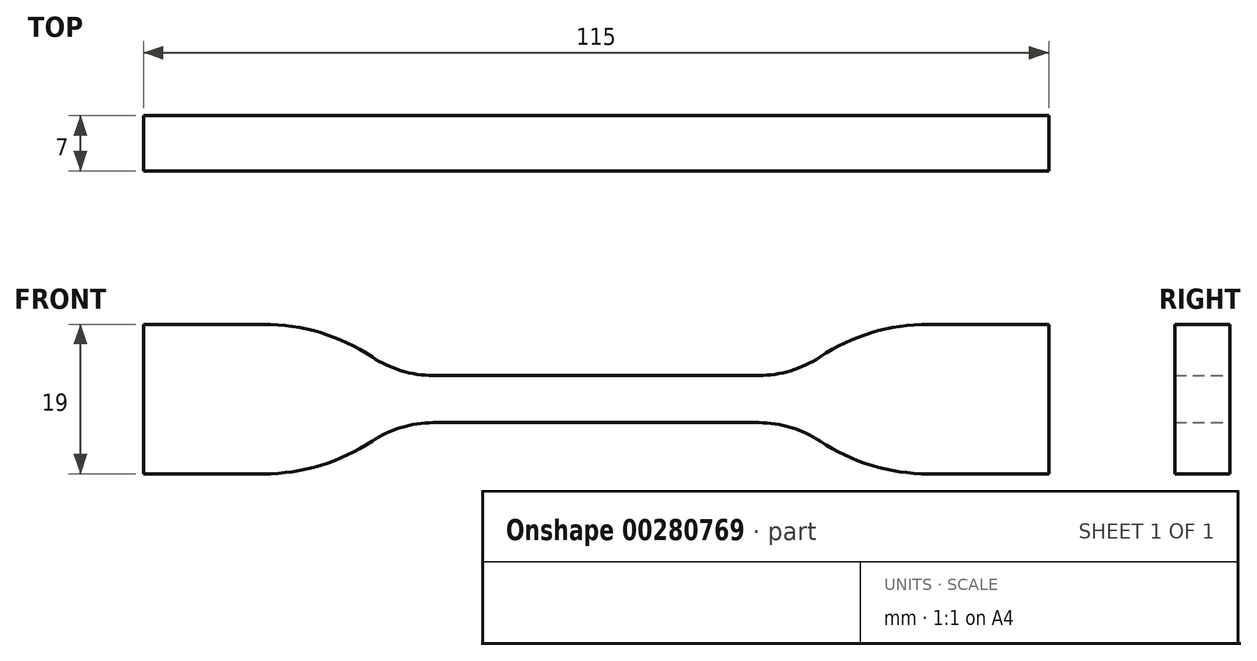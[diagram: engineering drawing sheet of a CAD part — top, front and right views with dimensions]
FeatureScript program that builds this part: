
annotation { "Feature Type Name" : "Feature", "Feature Type Description" : "" }
export const myFeature = defineFeature(function(context is Context, id is Id, definition is map)
    precondition{}
    {
        {
            var Q0;
            Q0=qCreatedBy(makeId("Front.planeOp"),FACE);
            var sketch = newSketch(context, id + "F0", { "sketchPlane" : qUnion([Q0])});
            skLineSegment(sketch, "E0", {"start": v(0, 3) * mm, "end": v(20.68, 3) * mm});
            skArc(sketch, "E1", {"start": v(20.68, 3) * mm, "mid": v(24.72, 3.6) * mm, "end": v(28.42, 5.33) * mm});
            skLineSegment(sketch, "E2", {"start": v(57.5, 9.5) * mm, "end": v(42.24, 9.5) * mm});
            skLineSegment(sketch, "E3.MirrorCS", {"start": v(57.5, -9.5) * mm, "end": v(42.24, -9.5) * mm});
            skLineSegment(sketch, "E4.MirrorCS", {"start": v(0, -3) * mm, "end": v(20.68, -3) * mm});
            skArc(sketch, "E5.MirrorCS", {"start": v(20.68, -3) * mm, "mid": v(24.72, -3.6) * mm, "end": v(28.42, -5.33) * mm});
            skLineSegment(sketch, "E6", {"start": v(57.5, 9.5) * mm, "end": v(57.5, -9.5) * mm});
            skLineSegment(sketch, "E7.MirrorCS", {"start": v(0, 3) * mm, "end": v(-20.68, 3) * mm});
            skArc(sketch, "E8.MirrorCS", {"start": v(-20.68, 3) * mm, "mid": v(-24.72, 3.6) * mm, "end": v(-28.42, 5.33) * mm});
            skLineSegment(sketch, "E9.MirrorCS", {"start": v(-57.5, 9.5) * mm, "end": v(-42.24, 9.5) * mm});
            skLineSegment(sketch, "E10.MirrorCS", {"start": v(-57.5, -9.5) * mm, "end": v(-42.24, -9.5) * mm});
            skLineSegment(sketch, "E11.MirrorCS", {"start": v(-57.5, 9.5) * mm, "end": v(-57.5, -9.5) * mm});
            skLineSegment(sketch, "E12.MirrorCS", {"start": v(0, -3) * mm, "end": v(-20.68, -3) * mm});
            skArc(sketch, "E13.MirrorCS", {"start": v(-20.68, -3) * mm, "mid": v(-24.72, -3.6) * mm, "end": v(-28.42, -5.33) * mm});
            skPoint(sketch, "E14.visualSharp", {"position": v(-32.5, -9.5) * mm});
            skArc(sketch, "E14.filletArc", {"start": v(-42.24, -9.5) * mm, "mid": v(-35.02, -8.44) * mm, "end": v(-28.42, -5.33) * mm});
            skPoint(sketch, "E15.visualSharp", {"position": v(-32.5, 9.5) * mm});
            skArc(sketch, "E15.filletArc", {"start": v(-28.42, 5.33) * mm, "mid": v(-35.02, 8.44) * mm, "end": v(-42.24, 9.5) * mm});
            skPoint(sketch, "E16.visualSharp", {"position": v(32.5, 9.5) * mm});
            skArc(sketch, "E16.filletArc", {"start": v(42.24, 9.5) * mm, "mid": v(35.02, 8.44) * mm, "end": v(28.42, 5.33) * mm});
            skPoint(sketch, "E17.visualSharp", {"position": v(32.5, -9.5) * mm});
            skArc(sketch, "E17.filletArc", {"start": v(28.42, -5.33) * mm, "mid": v(35.02, -8.44) * mm, "end": v(42.24, -9.5) * mm});
            skSolve(sketch);
        }
        {
            var Q0;
            Q0=makeQuery(id+"F0.imprint","IMPRINT",FACE,{"disambiguationData":[TD([[makeQuery(id+"F0.imprint","IMPRINT",EDGE,{"derivedFrom":sQuery(id+"F0.wireOp",EDGE,"E0")}),-1.0]])]});
            extrude(context, id + "F1", {"entities" : qUnion([Q0]), "endBound" : BoundingType.SYMMETRIC, "depth" : 7 * mm});
        }
    });
